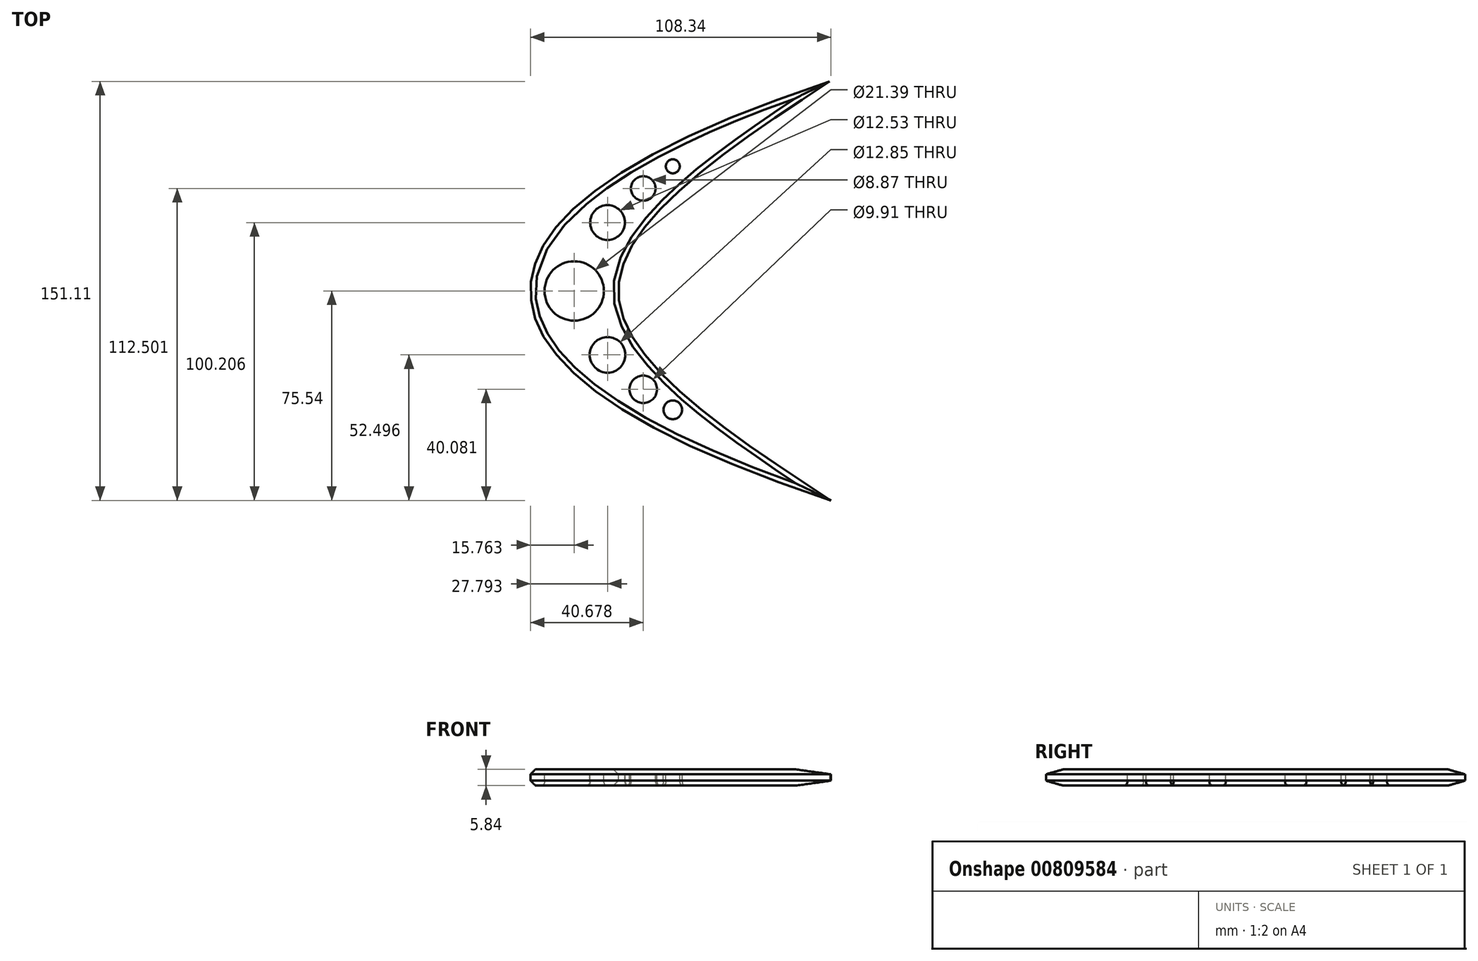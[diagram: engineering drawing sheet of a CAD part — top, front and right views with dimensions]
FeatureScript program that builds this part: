
annotation { "Feature Type Name" : "Feature", "Feature Type Description" : "" }
export const myFeature = defineFeature(function(context is Context, id is Id, definition is map)
    precondition{}
    {
        {
            var Q0;
            Q0=qCreatedBy(makeId("Top.planeOp"),FACE);
            var sketch = newSketch(context, id + "F0", { "sketchPlane" : qUnion([Q0])});
            skFitSpline(sketch, "E0", {"points": [v(76.67, -75.54) * mm, v(-31.67, 0) * mm, v(76.18, 75.56) * mm], "startDerivative": vector(-455.93, 150.92) * mm, "endDerivative": vector(455.13, 151.29) * mm});
            skFitSpline(sketch, "E1", {"points": [v(76.67, -75.54) * mm, v(0, 0) * mm, v(76.18, 75.56) * mm], "startDerivative": vector(-229.71, 150.89) * mm, "endDerivative": vector(228.84, 151.32) * mm});
            skSolve(sketch);
        }
        {
            var Q0;
            Q0=makeQuery(id+"F0.imprint","IMPRINT",FACE,{"disambiguationData":[TD([[makeQuery(id+"F0.imprint","IMPRINT",EDGE,{"derivedFrom":sQuery(id+"F0.wireOp",EDGE,"E0")}),-1.0]])]});
            var Q1;
            Q1 = qSketchRegion(id + "F3", true);
            extrude(context, id + "F1", {"entities" : qUnion([Q0, Q1]), "depth" : 5.84 * mm, "offsetDistance" : 25.4 * mm});
        }
        {
            var Q0;
            Q0=makeQuery(id+"F1.opExtrude","CAP_EDGE",EDGE,{"disambiguationData":[OSD([sQuery(id+"F0.wireOp",EDGE,"E0")])],"isStart":false});
            var Q1;
            Q1=makeQuery(id+"F1.opExtrude","CAP_EDGE",EDGE,{"disambiguationData":[OSD([sQuery(id+"F0.wireOp",EDGE,"E0")])],"isStart":true});
            var Q2;
            Q2=makeQuery(id+"F1.opExtrude","CAP_EDGE",EDGE,{"disambiguationData":[OSD([sQuery(id+"F0.wireOp",EDGE,"E1")])],"isStart":false});
            var Q3;
            Q3=makeQuery(id+"F1.opExtrude","CAP_EDGE",EDGE,{"disambiguationData":[OSD([sQuery(id+"F0.wireOp",EDGE,"E1")])],"isStart":true});
            chamfer(context, id + "F2", {"entities" : qUnion([Q0, Q1, Q2, Q3]), "width" : 1.78 * mm, "tangentPropagation" : true});
        }
        {
            var Q0;
            Q0=makeQuery(id+"F1.opExtrude","CAP_FACE",FACE,{"disambiguationData":[OSD([sQuery(id+"F0.wireOp",EDGE,"E0"),sQuery(id+"F0.wireOp",EDGE,"E1")])],"isStart":false});
            var sketch = newSketch(context, id + "F3", { "sketchPlane" : qUnion([Q0])});
            skCircle(sketch, "E2", {"center": v(-15.9, 0) * mm, "radius": 10.7 * mm});
            skCircle(sketch, "E3", {"center": v(-3.88, 24.67) * mm, "radius": 6.26 * mm});
            skCircle(sketch, "E4", {"center": v(-3.88, -23.04) * mm, "radius": 6.42 * mm});
            skSolve(sketch);
        }
        {
            var Q0;
            Q0=makeQuery(id+"F3.imprint","IMPRINT",FACE,{"disambiguationData":[TD([[makeQuery(id+"F3.imprint","IMPRINT",EDGE,{"derivedFrom":sQuery(id+"F3.wireOp",EDGE,"E2")}),1.0]])]});
            var Q1;
            Q1=makeQuery(id+"F3.imprint","IMPRINT",FACE,{"disambiguationData":[TD([[makeQuery(id+"F3.imprint","IMPRINT",EDGE,{"derivedFrom":sQuery(id+"F3.wireOp",EDGE,"E3")}),1.0]])]});
            var Q2;
            Q2=makeQuery(id+"F3.imprint","IMPRINT",FACE,{"disambiguationData":[TD([[makeQuery(id+"F3.imprint","IMPRINT",EDGE,{"derivedFrom":sQuery(id+"F3.wireOp",EDGE,"E4")}),1.0]])]});
            extrude(context, id + "F4", {"entities" : qUnion([Q0, Q1, Q2]), "operationType" : NewBodyOperationType.REMOVE, "oppositeDirection" : true, "depth" : 53.1 * mm, "offsetDistance" : 25.4 * mm});
        }
        {
            var Q0;
            Q0=makeQuery(id+"F1.opExtrude","CAP_FACE",FACE,{"disambiguationData":[OSD([sQuery(id+"F0.wireOp",EDGE,"E0"),sQuery(id+"F0.wireOp",EDGE,"E1")])],"isStart":false});
            var sketch = newSketch(context, id + "F5", { "sketchPlane" : qUnion([Q0])});
            skCircle(sketch, "E5", {"center": v(9, 36.96) * mm, "radius": 4.43 * mm});
            skCircle(sketch, "E6", {"center": v(9, -35.46) * mm, "radius": 4.96 * mm});
            skCircle(sketch, "E7", {"center": v(19.65, 44.94) * mm, "radius": 2.53 * mm});
            skCircle(sketch, "E8", {"center": v(19.65, -42.85) * mm, "radius": 3.37 * mm});
            skSolve(sketch);
        }
        {
            var Q0;
            Q0 = qSketchRegion(id + "F5", true);
            extrude(context, id + "F6", {"entities" : qUnion([Q0]), "operationType" : NewBodyOperationType.REMOVE, "oppositeDirection" : true, "depth" : 25.4 * mm, "offsetDistance" : 25.4 * mm});
        }
        {
            var Q0;
            Q0=makeQuery(id+"F6.boolean.opBoolean","COPY",EDGE,{"derivedFrom":makeQuery(id+"F6.opExtrude","CAP_EDGE",EDGE,{"disambiguationData":[OSD([sQuery(id+"F5.wireOp",EDGE,"E7")])],"isStart":true})});
            var Q1;
            Q1=makeQuery(id+"F6.boolean.opBoolean","COPY",EDGE,{"derivedFrom":makeQuery(id+"F6.opExtrude","CAP_EDGE",EDGE,{"disambiguationData":[OSD([sQuery(id+"F5.wireOp",EDGE,"E5")])],"isStart":true})});
            var Q2;
            Q2=makeQuery(id+"F4.boolean.opBoolean","COPY",EDGE,{"derivedFrom":makeQuery(id+"F4.opExtrude","CAP_EDGE",EDGE,{"disambiguationData":[OSD([sQuery(id+"F3.wireOp",EDGE,"E3")])],"isStart":true})});
            var Q3;
            Q3=makeQuery(id+"F4.boolean.opBoolean","COPY",EDGE,{"derivedFrom":makeQuery(id+"F4.opExtrude","CAP_EDGE",EDGE,{"disambiguationData":[OSD([sQuery(id+"F3.wireOp",EDGE,"E2")])],"isStart":true})});
            var Q4;
            Q4=makeQuery(id+"F4.boolean.opBoolean","COPY",EDGE,{"derivedFrom":makeQuery(id+"F4.opExtrude","CAP_EDGE",EDGE,{"disambiguationData":[OSD([sQuery(id+"F3.wireOp",EDGE,"E4")])],"isStart":true})});
            var Q5;
            Q5=makeQuery(id+"F6.boolean.opBoolean","COPY",EDGE,{"derivedFrom":makeQuery(id+"F6.opExtrude","CAP_EDGE",EDGE,{"disambiguationData":[OSD([sQuery(id+"F5.wireOp",EDGE,"E6")])],"isStart":true})});
            var Q6;
            Q6=makeQuery(id+"F6.boolean.opBoolean","COPY",EDGE,{"derivedFrom":makeQuery(id+"F6.opExtrude","CAP_EDGE",EDGE,{"disambiguationData":[OSD([sQuery(id+"F5.wireOp",EDGE,"E8")])],"isStart":true})});
            var Q7;
            Q7=makeQuery(id+"F6.boolean.opBoolean","INTERSECT",EDGE,{"derivedFrom":[makeQuery(id+"F1.opExtrude","CAP_FACE",FACE,{"disambiguationData":[OSD([sQuery(id+"F0.wireOp",EDGE,"E0"),sQuery(id+"F0.wireOp",EDGE,"E1")])],"isStart":true}),makeQuery(id+"F6.opExtrude","SWEPT_FACE",FACE,{"disambiguationData":[OSD([sQuery(id+"F5.wireOp",EDGE,"E7")])]})]});
            var Q8;
            Q8=makeQuery(id+"F6.boolean.opBoolean","INTERSECT",EDGE,{"derivedFrom":[makeQuery(id+"F1.opExtrude","CAP_FACE",FACE,{"disambiguationData":[OSD([sQuery(id+"F0.wireOp",EDGE,"E0"),sQuery(id+"F0.wireOp",EDGE,"E1")])],"isStart":true}),makeQuery(id+"F6.opExtrude","SWEPT_FACE",FACE,{"disambiguationData":[OSD([sQuery(id+"F5.wireOp",EDGE,"E5")])]})]});
            var Q9;
            Q9=makeQuery(id+"F4.boolean.opBoolean","INTERSECT",EDGE,{"derivedFrom":[makeQuery(id+"F1.opExtrude","CAP_FACE",FACE,{"disambiguationData":[OSD([sQuery(id+"F0.wireOp",EDGE,"E0"),sQuery(id+"F0.wireOp",EDGE,"E1")])],"isStart":true}),makeQuery(id+"F4.opExtrude","SWEPT_FACE",FACE,{"disambiguationData":[OSD([sQuery(id+"F3.wireOp",EDGE,"E3")])]})]});
            var Q10;
            Q10=makeQuery(id+"F4.boolean.opBoolean","INTERSECT",EDGE,{"derivedFrom":[makeQuery(id+"F1.opExtrude","CAP_FACE",FACE,{"disambiguationData":[OSD([sQuery(id+"F0.wireOp",EDGE,"E0"),sQuery(id+"F0.wireOp",EDGE,"E1")])],"isStart":true}),makeQuery(id+"F4.opExtrude","SWEPT_FACE",FACE,{"disambiguationData":[OSD([sQuery(id+"F3.wireOp",EDGE,"E2")])]})]});
            var Q11;
            Q11=makeQuery(id+"F4.boolean.opBoolean","INTERSECT",EDGE,{"derivedFrom":[makeQuery(id+"F1.opExtrude","CAP_FACE",FACE,{"disambiguationData":[OSD([sQuery(id+"F0.wireOp",EDGE,"E0"),sQuery(id+"F0.wireOp",EDGE,"E1")])],"isStart":true}),makeQuery(id+"F4.opExtrude","SWEPT_FACE",FACE,{"disambiguationData":[OSD([sQuery(id+"F3.wireOp",EDGE,"E4")])]})]});
            var Q12;
            Q12=makeQuery(id+"F6.boolean.opBoolean","INTERSECT",EDGE,{"derivedFrom":[makeQuery(id+"F1.opExtrude","CAP_FACE",FACE,{"disambiguationData":[OSD([sQuery(id+"F0.wireOp",EDGE,"E0"),sQuery(id+"F0.wireOp",EDGE,"E1")])],"isStart":true}),makeQuery(id+"F6.opExtrude","SWEPT_FACE",FACE,{"disambiguationData":[OSD([sQuery(id+"F5.wireOp",EDGE,"E6")])]})]});
            var Q13;
            Q13=makeQuery(id+"F6.boolean.opBoolean","INTERSECT",EDGE,{"derivedFrom":[makeQuery(id+"F1.opExtrude","CAP_FACE",FACE,{"disambiguationData":[OSD([sQuery(id+"F0.wireOp",EDGE,"E0"),sQuery(id+"F0.wireOp",EDGE,"E1")])],"isStart":true}),makeQuery(id+"F6.opExtrude","SWEPT_FACE",FACE,{"disambiguationData":[OSD([sQuery(id+"F5.wireOp",EDGE,"E8")])]})]});
            fillet(context, id + "F7", {"entities" : qUnion([Q0, Q1, Q2, Q3, Q4, Q5, Q6, Q7, Q8, Q9, Q10, Q11, Q12, Q13]), "radius" : 1.27 * mm, "tangentPropagation" : true, "allowEdgeOverflow" : false});
        }
    });
